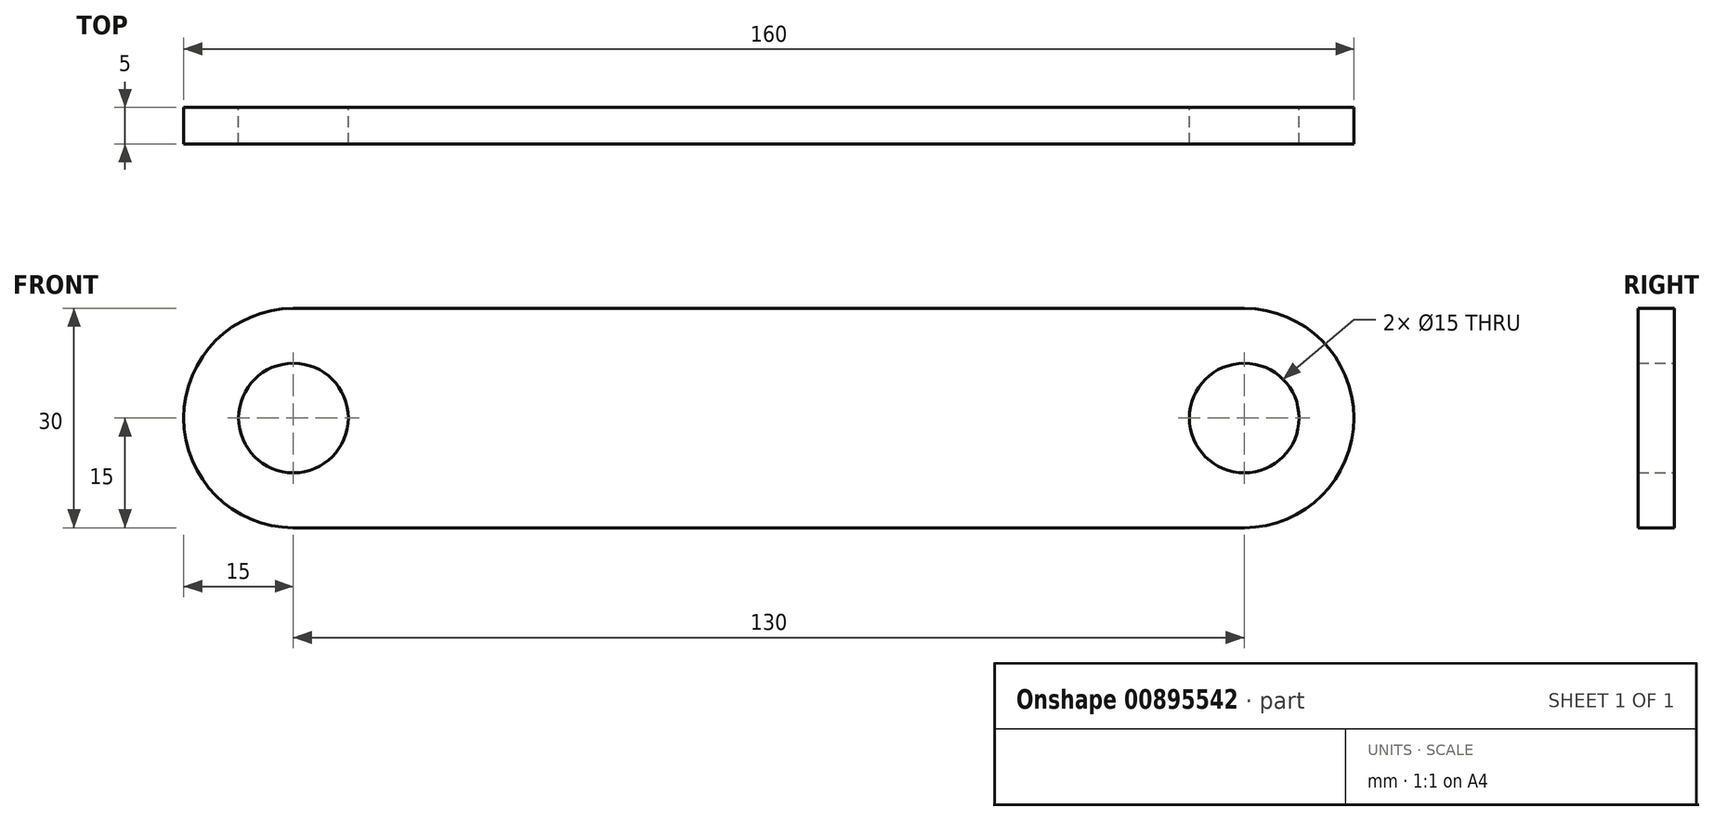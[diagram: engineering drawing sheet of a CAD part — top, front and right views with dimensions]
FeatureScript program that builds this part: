
annotation { "Feature Type Name" : "Feature", "Feature Type Description" : "" }
export const myFeature = defineFeature(function(context is Context, id is Id, definition is map)
    precondition{}
    {
        {
            var Q0;
            Q0=qCreatedBy(makeId("Front.planeOp"),FACE);
            var sketch = newSketch(context, id + "F0", { "sketchPlane" : qUnion([Q0])});
            skArc(sketch, "E0", {"start": v(0, 15) * mm, "mid": v(-15, 0) * mm, "end": v(0, -15) * mm});
            skCircle(sketch, "E1", {"center": v(0, 0) * mm, "radius": 7.5 * mm});
            skCircle(sketch, "E2", {"center": v(130, 0) * mm, "radius": 7.5 * mm});
            skArc(sketch, "E3", {"start": v(130, -15) * mm, "mid": v(145, 0) * mm, "end": v(130, 15) * mm});
            skLineSegment(sketch, "E4", {"start": v(0, 15) * mm, "end": v(130, 15) * mm});
            skLineSegment(sketch, "E5", {"start": v(0, -15) * mm, "end": v(130, -15) * mm});
            skSolve(sketch);
        }
        {
            var Q0;
            Q0=makeQuery(id+"F0.imprint","IMPRINT",FACE,{"disambiguationData":[TD([[makeQuery(id+"F0.imprint","IMPRINT",EDGE,{"derivedFrom":sQuery(id+"F0.wireOp",EDGE,"E0")}),1.0]])]});
            extrude(context, id + "F1", {"entities" : qUnion([Q0]), "depth" : 5 * mm, "offsetDistance" : 25 * mm});
        }
    });
